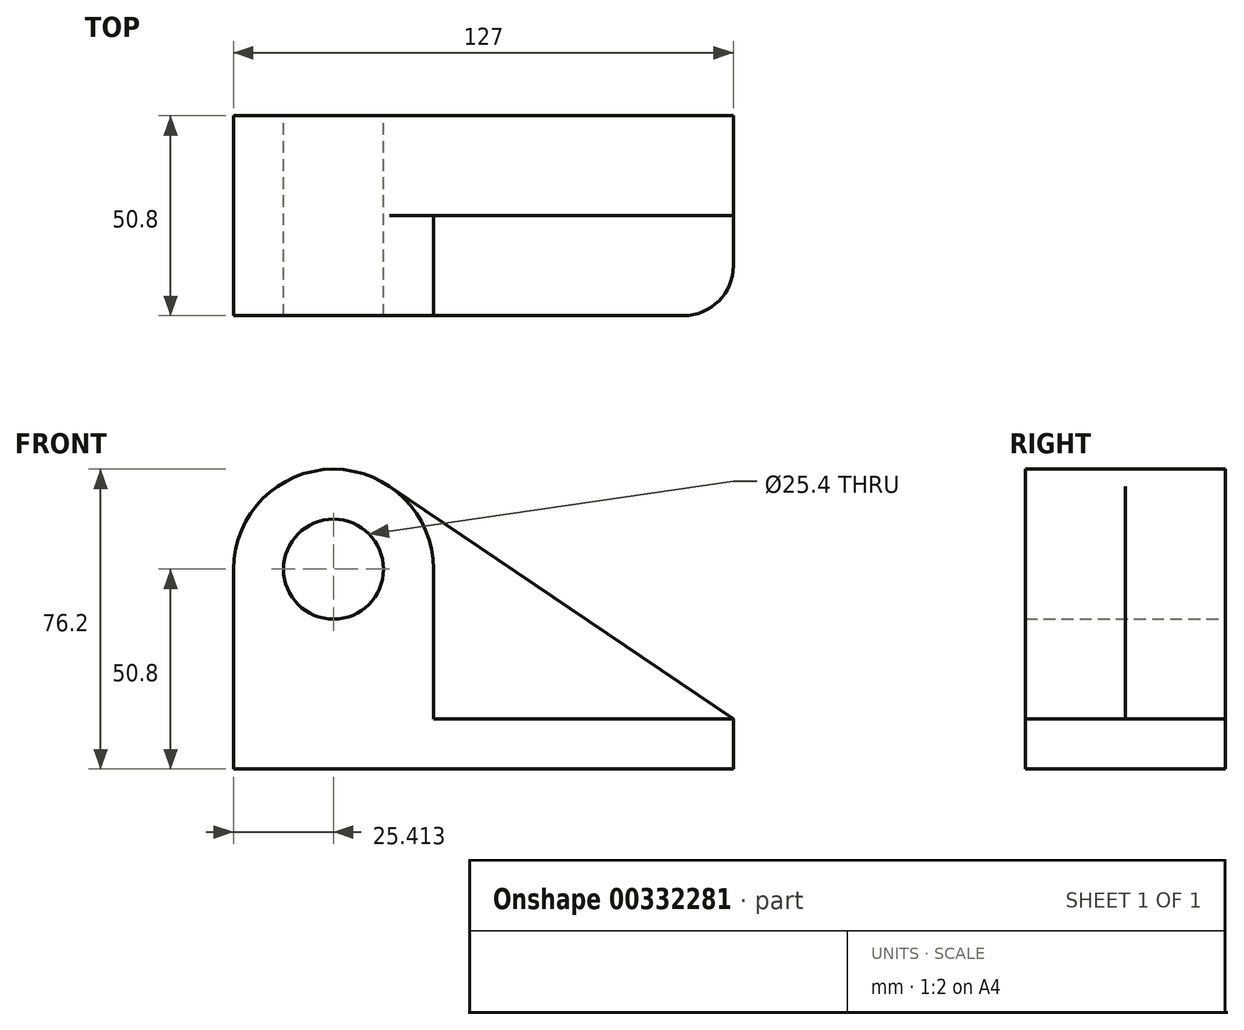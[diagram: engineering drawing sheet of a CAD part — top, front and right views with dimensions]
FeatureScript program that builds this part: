
annotation { "Feature Type Name" : "Feature", "Feature Type Description" : "" }
export const myFeature = defineFeature(function(context is Context, id is Id, definition is map)
    precondition{}
    {
        {
            var Q0;
            Q0=qCreatedBy(makeId("Front.planeOp"),FACE);
            var sketch = newSketch(context, id + "F0", { "sketchPlane" : qUnion([Q0])});
            skCircle(sketch, "E0", {"center": v(-41.62, 50.8) * mm, "radius": 12.7 * mm});
            skArc(sketch, "E1", {"start": v(-27.38, 71.83) * mm, "mid": v(-53.52, 73.24) * mm, "end": v(-67.02, 50.8) * mm});
            skLineSegment(sketch, "E2", {"start": v(-67.02, 50.8) * mm, "end": v(-67.03, 0) * mm});
            skLineSegment(sketch, "E3", {"start": v(-67.03, 0) * mm, "end": v(59.97, 0) * mm});
            skLineSegment(sketch, "E4", {"start": v(59.97, 0) * mm, "end": v(59.97, 12.7) * mm});
            skLineSegment(sketch, "E5", {"start": v(59.97, 12.7) * mm, "end": v(-27.38, 71.83) * mm});
            skArc(sketch, "E6", {"start": v(-16.22, 50.8) * mm, "mid": v(-41.62, 76.2) * mm, "end": v(-67.02, 50.8) * mm});
            skLineSegment(sketch, "E7.bottom", {"start": v(59.97, 12.7) * mm, "end": v(-16.22, 12.7) * mm});
            skLineSegment(sketch, "E7.top", {"start": v(59.97, 12.7) * mm, "end": v(-16.22, 12.7) * mm});
            skLineSegment(sketch, "E7.left", {"start": v(59.97, 12.7) * mm, "end": v(59.97, 12.7) * mm});
            skLineSegment(sketch, "E7.right", {"start": v(-67.02, 12.7) * mm, "end": v(-67.02, 12.7) * mm});
            skLineSegment(sketch, "E8", {"start": v(-67.02, 50.8) * mm, "end": v(-67.02, 12.7) * mm});
            skLineSegment(sketch, "E9", {"start": v(-16.22, 50.8) * mm, "end": v(-16.22, 12.7) * mm});
            skSolve(sketch);
        }
        {
            var Q0;
            Q0 = qSketchRegion(id + "F0", true);
            extrude(context, id + "F1", {"entities" : qUnion([Q0]), "depth" : 25.4 * mm});
        }
        {
            var Q0;
            Q0=makeQuery(id+"F0.imprint","IMPRINT",FACE,{"disambiguationData":[TD([[makeQuery(id+"F0.imprint","IMPRINT",EDGE,{"derivedFrom":sQuery(id+"F0.wireOp",EDGE,"E0")}),-1.0]])]});
            extrude(context, id + "F2", {"entities" : qUnion([Q0]), "operationType" : NewBodyOperationType.ADD, "depth" : 50.8 * mm});
        }
        {
            var Q0;
            Q0=makeQuery(id+"F2.opExtrude","CAP_EDGE",EDGE,{"disambiguationData":[OSD([sQuery(id+"F0.wireOp",EDGE,"E4")])],"isStart":false});
            fillet(context, id + "F3", {"entities" : qUnion([Q0]), "radius" : 12.7 * mm, "tangentPropagation" : true, "allowEdgeOverflow" : false});
        }
    });
